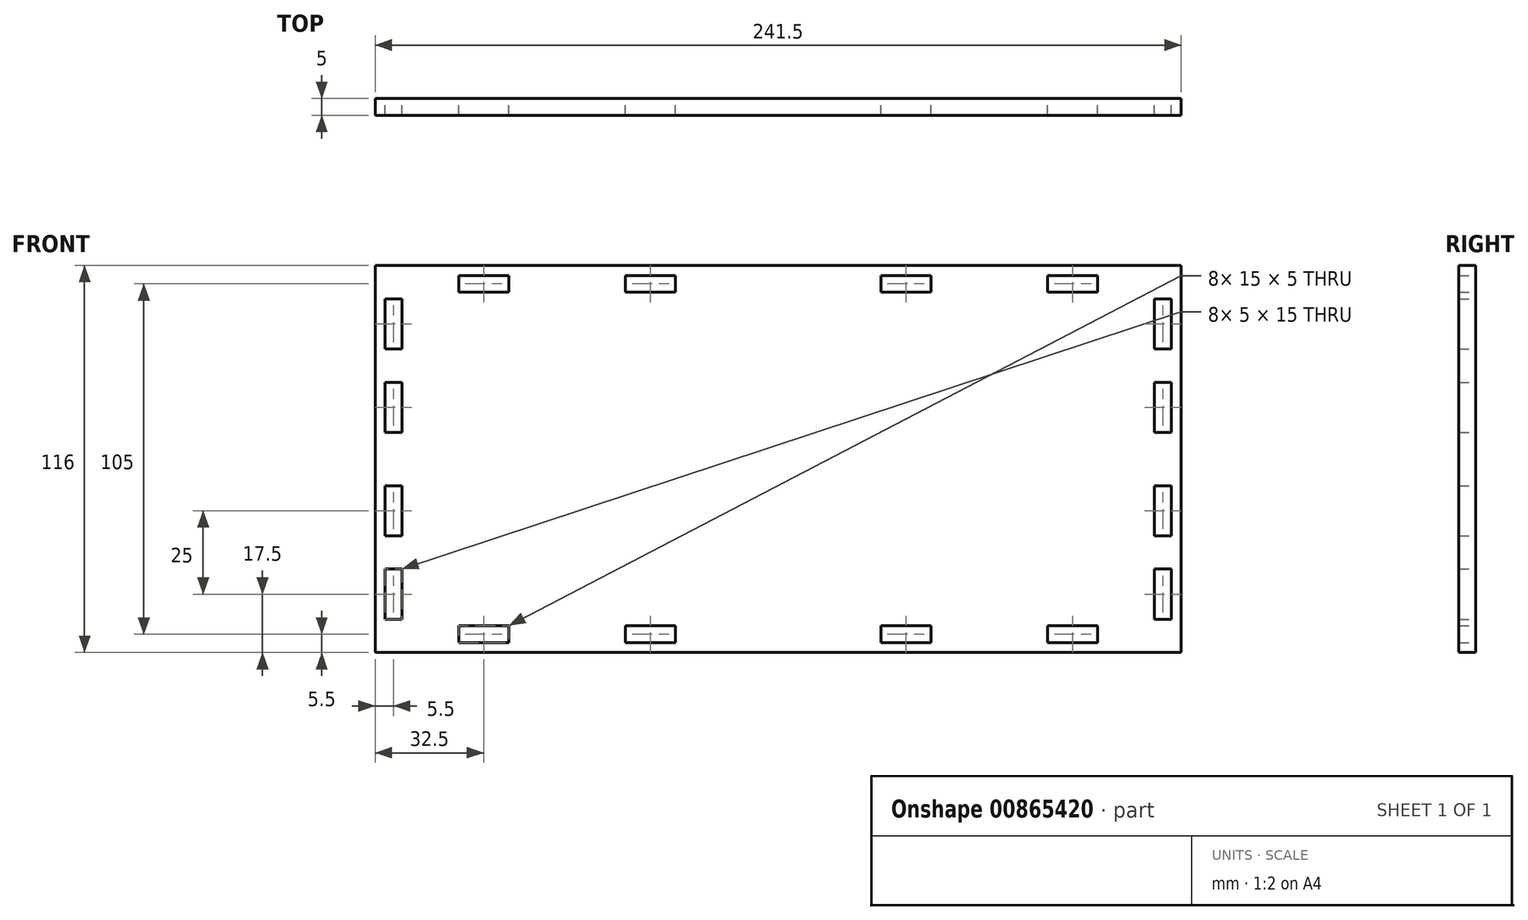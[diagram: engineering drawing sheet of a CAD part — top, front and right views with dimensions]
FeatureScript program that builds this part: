
annotation { "Feature Type Name" : "Feature", "Feature Type Description" : "" }
export const myFeature = defineFeature(function(context is Context, id is Id, definition is map)
    precondition{}
    {
        {
            var Q0;
            Q0=qCreatedBy(makeId("Front.planeOp"),FACE);
            var sketch = newSketch(context, id + "F0", { "sketchPlane" : qUnion([Q0])});
            skLineSegment(sketch, "E0.bottom", {"start": v(120.75, -58) * mm, "end": v(-120.75, -58) * mm});
            skLineSegment(sketch, "E0.top", {"start": v(120.75, 58) * mm, "end": v(-120.75, 58) * mm});
            skLineSegment(sketch, "E0.left", {"start": v(120.75, -58) * mm, "end": v(120.75, 58) * mm});
            skLineSegment(sketch, "E0.right", {"start": v(-120.75, -58) * mm, "end": v(-120.75, 58) * mm});
            skPoint(sketch, "E0.middle", {"position": v(0, 0) * mm});
            skLineSegment(sketch, "E1.bottom", {"start": v(-80.75, 50) * mm, "end": v(-95.75, 50) * mm});
            skLineSegment(sketch, "E1.top", {"start": v(-80.75, 55) * mm, "end": v(-95.75, 55) * mm});
            skLineSegment(sketch, "E1.left", {"start": v(-80.75, 50) * mm, "end": v(-80.75, 55) * mm});
            skLineSegment(sketch, "E1.right", {"start": v(-95.75, 50) * mm, "end": v(-95.75, 55) * mm});
            skPoint(sketch, "E1.middle", {"position": v(-88.25, 52.5) * mm});
            skLineSegment(sketch, "E2.bottom", {"start": v(-30.75, 50) * mm, "end": v(-45.75, 50) * mm});
            skLineSegment(sketch, "E2.top", {"start": v(-30.75, 55) * mm, "end": v(-45.75, 55) * mm});
            skLineSegment(sketch, "E2.left", {"start": v(-30.75, 50) * mm, "end": v(-30.75, 55) * mm});
            skLineSegment(sketch, "E2.right", {"start": v(-45.75, 50) * mm, "end": v(-45.75, 55) * mm});
            skPoint(sketch, "E2.middle", {"position": v(-38.25, 52.5) * mm});
            skLineSegment(sketch, "E3.MirrorCS", {"start": v(30.75, 50) * mm, "end": v(45.75, 50) * mm});
            skLineSegment(sketch, "E4.MirrorCS", {"start": v(30.75, 55) * mm, "end": v(45.75, 55) * mm});
            skLineSegment(sketch, "E5.MirrorCS", {"start": v(30.75, 50) * mm, "end": v(30.75, 55) * mm});
            skLineSegment(sketch, "E6.MirrorCS", {"start": v(45.75, 50) * mm, "end": v(45.75, 55) * mm});
            skLineSegment(sketch, "E7.MirrorCS", {"start": v(80.75, 50) * mm, "end": v(80.75, 55) * mm});
            skLineSegment(sketch, "E8.MirrorCS", {"start": v(80.75, 55) * mm, "end": v(95.75, 55) * mm});
            skLineSegment(sketch, "E9.MirrorCS", {"start": v(95.75, 50) * mm, "end": v(95.75, 55) * mm});
            skLineSegment(sketch, "E10.MirrorCS", {"start": v(80.75, 50) * mm, "end": v(95.75, 50) * mm});
            skLineSegment(sketch, "E11.MirrorCS", {"start": v(-80.75, -50) * mm, "end": v(-95.75, -50) * mm});
            skLineSegment(sketch, "E12.MirrorCS", {"start": v(-80.75, -55) * mm, "end": v(-95.75, -55) * mm});
            skLineSegment(sketch, "E13.MirrorCS", {"start": v(-80.75, -50) * mm, "end": v(-80.75, -55) * mm});
            skLineSegment(sketch, "E14.MirrorCS", {"start": v(-95.75, -50) * mm, "end": v(-95.75, -55) * mm});
            skLineSegment(sketch, "E15.MirrorCS", {"start": v(-45.75, -50) * mm, "end": v(-45.75, -55) * mm});
            skLineSegment(sketch, "E16.MirrorCS", {"start": v(-30.75, -55) * mm, "end": v(-45.75, -55) * mm});
            skLineSegment(sketch, "E17.MirrorCS", {"start": v(-30.75, -50) * mm, "end": v(-30.75, -55) * mm});
            skLineSegment(sketch, "E18.MirrorCS", {"start": v(-30.75, -50) * mm, "end": v(-45.75, -50) * mm});
            skLineSegment(sketch, "E19.MirrorCS", {"start": v(30.75, -50) * mm, "end": v(30.75, -55) * mm});
            skLineSegment(sketch, "E20.MirrorCS", {"start": v(30.75, -55) * mm, "end": v(45.75, -55) * mm});
            skLineSegment(sketch, "E21.MirrorCS", {"start": v(45.75, -50) * mm, "end": v(45.75, -55) * mm});
            skLineSegment(sketch, "E22.MirrorCS", {"start": v(30.75, -50) * mm, "end": v(45.75, -50) * mm});
            skLineSegment(sketch, "E23.MirrorCS", {"start": v(80.75, -50) * mm, "end": v(80.75, -55) * mm});
            skLineSegment(sketch, "E24.MirrorCS", {"start": v(80.75, -55) * mm, "end": v(95.75, -55) * mm});
            skLineSegment(sketch, "E25.MirrorCS", {"start": v(95.75, -50) * mm, "end": v(95.75, -55) * mm});
            skLineSegment(sketch, "E26.MirrorCS", {"start": v(80.75, -50) * mm, "end": v(95.75, -50) * mm});
            skLineSegment(sketch, "E27.bottom", {"start": v(117.75, 33) * mm, "end": v(112.75, 33) * mm});
            skLineSegment(sketch, "E27.top", {"start": v(117.75, 48) * mm, "end": v(112.75, 48) * mm});
            skLineSegment(sketch, "E27.left", {"start": v(117.75, 33) * mm, "end": v(117.75, 48) * mm});
            skLineSegment(sketch, "E27.right", {"start": v(112.75, 33) * mm, "end": v(112.75, 48) * mm});
            skPoint(sketch, "E27.middle", {"position": v(115.25, 40.5) * mm});
            skLineSegment(sketch, "E28.bottom", {"start": v(117.75, 8) * mm, "end": v(112.75, 8) * mm});
            skLineSegment(sketch, "E28.top", {"start": v(117.75, 23) * mm, "end": v(112.75, 23) * mm});
            skLineSegment(sketch, "E28.left", {"start": v(117.75, 8) * mm, "end": v(117.75, 23) * mm});
            skLineSegment(sketch, "E28.right", {"start": v(112.75, 8) * mm, "end": v(112.75, 23) * mm});
            skPoint(sketch, "E28.middle", {"position": v(115.25, 15.5) * mm});
            skLineSegment(sketch, "E29.MirrorCS", {"start": v(117.75, -23) * mm, "end": v(112.75, -23) * mm});
            skLineSegment(sketch, "E30.MirrorCS", {"start": v(112.75, -8) * mm, "end": v(112.75, -23) * mm});
            skLineSegment(sketch, "E31.MirrorCS", {"start": v(117.75, -8) * mm, "end": v(117.75, -23) * mm});
            skLineSegment(sketch, "E32.MirrorCS", {"start": v(117.75, -8) * mm, "end": v(112.75, -8) * mm});
            skLineSegment(sketch, "E33.MirrorCS", {"start": v(117.75, -33) * mm, "end": v(112.75, -33) * mm});
            skLineSegment(sketch, "E34.MirrorCS", {"start": v(112.75, -33) * mm, "end": v(112.75, -48) * mm});
            skLineSegment(sketch, "E35.MirrorCS", {"start": v(117.75, -33) * mm, "end": v(117.75, -48) * mm});
            skLineSegment(sketch, "E36.MirrorCS", {"start": v(117.75, -48) * mm, "end": v(112.75, -48) * mm});
            skLineSegment(sketch, "E37.MirrorCS", {"start": v(-112.75, 33) * mm, "end": v(-112.75, 48) * mm});
            skLineSegment(sketch, "E38.MirrorCS", {"start": v(-117.75, 33) * mm, "end": v(-117.75, 48) * mm});
            skLineSegment(sketch, "E39.MirrorCS", {"start": v(-117.75, 33) * mm, "end": v(-112.75, 33) * mm});
            skLineSegment(sketch, "E40.MirrorCS", {"start": v(-117.75, 8) * mm, "end": v(-117.75, 23) * mm});
            skLineSegment(sketch, "E41.MirrorCS", {"start": v(-117.75, 8) * mm, "end": v(-112.75, 8) * mm});
            skLineSegment(sketch, "E42.MirrorCS", {"start": v(-112.75, -8) * mm, "end": v(-112.75, -23) * mm});
            skLineSegment(sketch, "E43.MirrorCS", {"start": v(-117.75, -8) * mm, "end": v(-117.75, -23) * mm});
            skLineSegment(sketch, "E44.MirrorCS", {"start": v(-117.75, -33) * mm, "end": v(-112.75, -33) * mm});
            skLineSegment(sketch, "E45.MirrorCS", {"start": v(-112.75, -33) * mm, "end": v(-112.75, -48) * mm});
            skLineSegment(sketch, "E46.MirrorCS", {"start": v(-117.75, -33) * mm, "end": v(-117.75, -48) * mm});
            skLineSegment(sketch, "E47.MirrorCS", {"start": v(-117.75, -48) * mm, "end": v(-112.75, -48) * mm});
            skLineSegment(sketch, "E48.MirrorCS", {"start": v(-117.75, -23) * mm, "end": v(-112.75, -23) * mm});
            skLineSegment(sketch, "E49.MirrorCS", {"start": v(-117.75, -8) * mm, "end": v(-112.75, -8) * mm});
            skLineSegment(sketch, "E50.MirrorCS", {"start": v(-117.75, 23) * mm, "end": v(-112.75, 23) * mm});
            skLineSegment(sketch, "E51.MirrorCS", {"start": v(-112.75, 8) * mm, "end": v(-112.75, 23) * mm});
            skLineSegment(sketch, "E52.MirrorCS", {"start": v(-117.75, 48) * mm, "end": v(-112.75, 48) * mm});
            skSolve(sketch);
        }
        {
            var Q0;
            Q0=makeQuery(id+"F0.imprint","IMPRINT",FACE,{"disambiguationData":[TD([[makeQuery(id+"F0.imprint","IMPRINT",EDGE,{"derivedFrom":sQuery(id+"F0.wireOp",EDGE,"E0.bottom")}),-1.0]])]});
            extrude(context, id + "F1", {"entities" : qUnion([Q0]), "depth" : 5 * mm, "offsetDistance" : 25 * mm});
        }
    });
